# Revit family: P1E_2863-2862-2606_OS265
name_source: partatom
category: Porte
units: mm (PartAtom-declared; Revit-internal decimal feet)

## family parameters
Condiviso = No
Host = Muro
Numero OmniClass = 23.30.10.00
Punto di calcolo locali = No
Sempre verticale = Sì
Taglio con vuoti quando caricato = No
Titolo OmniClass = Doors

## types (4) — shared parameters
Chiusura muro = Per host
Costruzione analitica = <Nessuno>
Descrizione = Porta ad un'anta, apertura esterna
Funzione = Interno
H_Max = 2900 mm
H_Min = 1600 mm
H_maniglia = 1000 mm  [stored 3.28084 ft]
L = 1000 mm  [stored 3.28084 ft]
L1 = 1000 mm  [stored 3.28084 ft]
L_Max = 1000 mm  [stored 3.28084 ft]
L_Min = 400 mm  [stored 1.31234 ft]
L_vetro = 924 mm  [stored 3.0315 ft]
Larghezza telaio = 75 mm
Modello = OS2 65
Produttore = Secco Sistemi Spa
Proiezione telaio est. = 25 mm  [stored 0.082021 ft]
Proiezione telaio int. = 25 mm  [stored 0.082021 ft]
URL = https://www.seccosistemi.com
n2_cerniere = 2
n3_cerniere = 3
n4_cerniere = 4
numero_cerniere = 3

## per-type parameters (varying)
| type | Altezza | H | H1 | H_vetro | Larghezza | MATERIALE | Nota tecnica | WARNING |
| Acciaio zincato | 2500 mm  [stored 8.2021 ft] | 2500 mm  [stored 8.2021 ft] | 2500 mm  [stored 8.2021 ft] | 2424 mm | 1100 mm | Acciaio |  | Sì |
| Acciaio inox | 2500 mm  [stored 8.2021 ft] | 2500 mm  [stored 8.2021 ft] | 2500 mm  [stored 8.2021 ft] | 2424 mm | 1100 mm | Acciaio inox, spazzolato |  | Sì |
| Acciaio Corten | 2000 mm  [stored 6.56168 ft] | 2000 mm  [stored 6.56168 ft] | 2000 mm  [stored 6.56168 ft] | 1924 mm | 1000 mm  [stored 3.28084 ft] | Acciaio corten | https://www.seccosistemi.com | No |
| Ottone | 2500 mm  [stored 8.2021 ft] | 2500 mm  [stored 8.2021 ft] | 2500 mm  [stored 8.2021 ft] | 2424 mm | 1100 mm | Ottone |  | Sì |

note: [stored X ft] marks values corroborated as IEEE doubles in the binary element streams (Revit-internal decimal feet)
